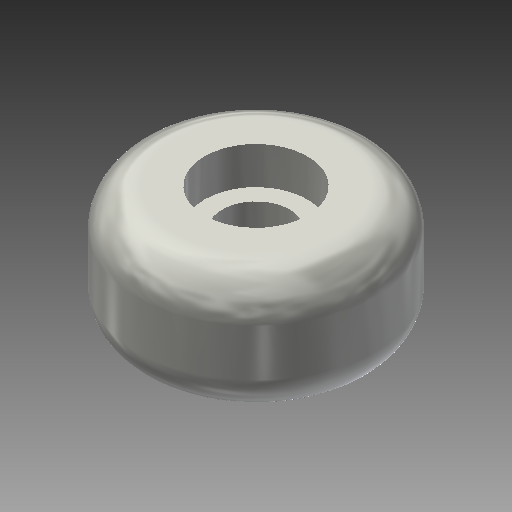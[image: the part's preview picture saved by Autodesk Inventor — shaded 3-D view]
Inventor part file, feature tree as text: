
AUTODESK INVENTOR PART (.ipt)
format: ipt  version: 2019 (Build 230136000, 136)  size: 179,200 bytes
history: native  units: mm
features: revolve x1, fillet x1, sketch x1
ambient origin geometry x8: Origin, YZ Plane, XZ Plane, XY Plane, X Axis, Y Axis, Z Axis, Center Point
bodies: Body1 (feature_tree)
feature tree (3):
  revolve  "Rivoluzione2"
  fillet  "Raccordo2"  Radius=7.25mm
  sketch  "Schizzo1"
